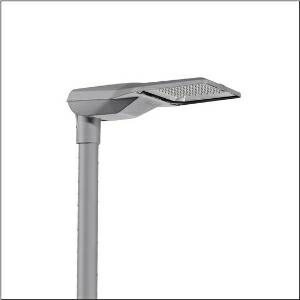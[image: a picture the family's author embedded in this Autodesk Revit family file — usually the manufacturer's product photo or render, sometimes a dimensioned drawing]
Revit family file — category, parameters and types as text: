
# Revit family: streetlight_sl_21_iq_midi___pc-r_5xe3g41g08mb_0911
name_source: partatom
category: Lighting Fixtures
units: mm (PartAtom-declared; Revit-internal decimal feet)

## family parameters
Cut with Voids When Loaded = No
Host = Face
Light Source = No
Part Type = Normal
Room Calculation Point = No
Round Connector Dimension = Use Diameter
Shared = No

## types (1)
- --- (1 x LED, 19370 lm, 146.7 W, 4000K)
    Apparent Load = 147 VA
    CIE Flux Codes = 38 78 98 100 100
    Color Rendering = 70
    Color Temperature = 4000K
    Default Elevation = 1800 mm
    Description = Streetlight SL 21 iQ midi, mast luminaire, primary light control with lens, of PMMA, primary optical cover: cover, of toughened safety glass, transparent, light distribution: PC-R, light emission: direct distribution, primary light characteristic: asymmetric, right, installation type: post-top, side-entry, LED, High Power LED, rated luminous flux: 19.370lm, luminous efficacy: 132lm/W, light colour: 740, colour temperature: 4000K, control gear: iQ Street-Remote, control: Street-Remote, Auto-Match, Temp-Guard, Lumen-Switch, Night-Set, Smart-Wire, Light-Fading, Desk-Remote (wireless, voltage-free reading and setting of iQ features in the workshop via application-optimized NFC function/RFID function), optimised constant luminous flux control (CLO 2.0), pre-setting: linear dimming characteristic, mains connection: 230..240V, AC, 50/60Hz, start of lifetime: 147W, end of service life: 161W, reduction: 62W, luminaire housing, of diecast aluminium, powder-coated, Siteco® metallic grey (DB 702S), corrosivity category C5 mid according to DIN EN ISO 12944, please order mast flange separately, inclination adjustable: 0°, 5°, 10°, 15°, sealing non-destructively replaceable, multi-level sealing system, length: 644mm, width: 335mm, height: 110mm, mast flange for spigot size: 42mm (side-entry): 5XC10008XM4, 60/48mm (side-entry/post-top): 5XC10108XM2, 76/60mm (side-entry/post-top): 5XC10108XM1, mounting height: 4..8m, protection rating (complete): IP66, insulation class (complete): insulation class II (safety insulation), certification: CE, ENEC, ENEC+, VDE, impact resistance: IK10, permissible operating ambient temperature for outdoor applications: -40..+50°C, standard-compliant lighting for roads and squares, packaging unit: 1 piece

Light Distribution: PC-R
    Height = 111 mm
    Lamp = 1 x LED
    Lamp Light Flux = 19370 lm
    Lamp Power = 146.7 W
    Lamp count = 1
    Length = 644 mm
    Luminous efficacy = 132 lm/W
    Manufacturer = Siteco
    ModVariant = No
    Model = 5XE3G41G08MB
    Number of Poles = 1
    OnlyDefault = Yes
    Power Factor = 1
    Product Name = Streetlight SL 21 iQ midi | PC-R
    Product group = mast luminaire | pylon top
    ProductGroupID = 6100
    Protection Class = Protection class II
    Protection Degree = IP 66
    RLX_Detail_Level = 1
    RLX_Emergency_Light_Flux = 0 lm
    RLX_Emergency_Type = 0
    RLX_Emergency_Type_DB = No
    RlxData = <blob elided: 29469 chars, md5=6e03e211>
    Socket = socket
    Standby Power = 0 W
    System Light Flux = 19370 lm
    System Power = 147 W
    Type Comments = factory setting: luminous flux: 100 % | dim-lin: 254 | 753 mA
    Type Image = l_1004298.jpg
    URL = http://relux.com
    VarID = @adj_085421
    Voltage = 0 V
    Weight = 0.00 kg
    Width = 336 mm

## geometry (parser evidence)
native form markers: Blend x4, Sweep x11
no freeform markers — native parametric forms only
